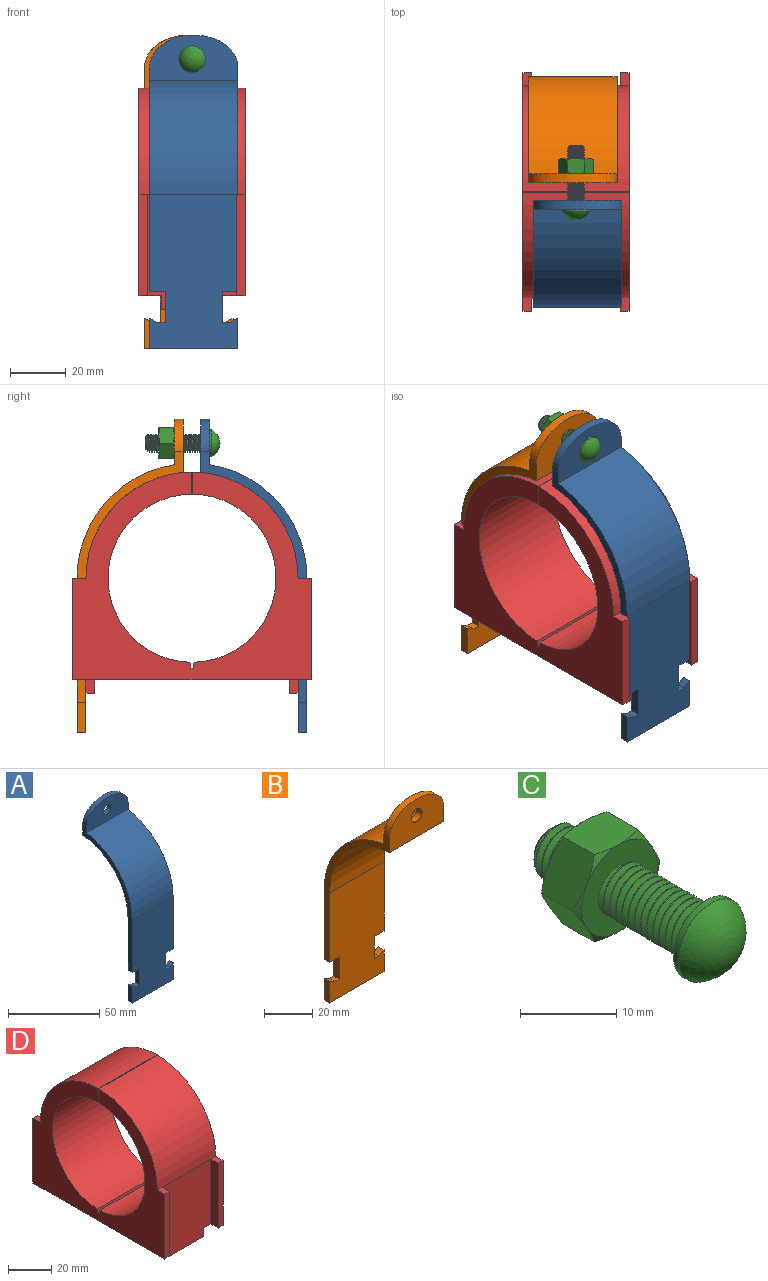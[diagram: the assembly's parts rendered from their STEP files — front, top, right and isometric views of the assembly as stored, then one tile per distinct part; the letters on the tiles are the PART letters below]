
ASSEMBLY  parts=4 mates=3
PART A: 21 faces, bbox 31.8x38.1x112.7 mm
  f0: plane 80.68x38.1mm, normal (-1,0,0), area 313.9mm2, adj f1,f13,f14,f15,f16,f17,f18,f20
  f1: plane 5.55x3.18mm, normal (0,0,-1), area 17.6mm2, adj f0,f2,f13,f16
  f2: plane 11.13x3.18mm, normal (-1,0,0), area 35.3mm2, adj f1,f3,f13,f16
  f3: plane 3.18x2.54mm, normal (0,0,1), area 8.1mm2, adj f2,f4,f13,f16
  f4: plane 3.18x3.01mm, normal (0.47,0,0.89), area 10.8mm2, adj f3,f5,f13,f16
  f5: plane 10.97x3.18mm, normal (-1,0,0), area 34.8mm2, adj f4,f6,f13,f16
  f6: plane 31.75x3.18mm, normal (0,0,-1), area 100.8mm2, adj f5,f7,f13,f16
  f7: plane 10.97x3.18mm, normal (1,0,0), area 34.8mm2, adj f6,f8,f13,f16
  f8: plane 3.18x3.01mm, normal (-0.47,0,0.89), area 10.8mm2, adj f7,f9,f13,f16
  f9: plane 3.18x2.54mm, normal (0,0,1), area 8.1mm2, adj f8,f10,f13,f16
  f10: plane 11.13x3.18mm, normal (1,0,0), area 35.3mm2, adj f9,f11,f13,f16
  f11: plane 5.55x3.18mm, normal (0,0,-1), area 17.6mm2, adj f10,f12,f13,f16
  f12: plane 80.68x38.1mm, normal (1,0,0), area 313.9mm2, adj f11,f13,f14,f15,f16,f17,f18,f20
  f13: plane 55.55x31.75mm, normal (0,-1,0), area 1645mm2, adj f0,f1,f2,f3,f4,f5,f6,f7
  f14: plane 31.75x16.38mm, normal (0,-1,0), area 409.9mm2, adj f0,f12,f15,f19,f20
  f15: cylinder r=41.27mm len=40.78mm, axis (1,0,0), area 1856.1mm2, adj f0,f12,f13,f14
  f16: plane 55.55x31.75mm, normal (0,1,0), area 1645mm2, adj f0,f1,f2,f3,f4,f5,f6,f7
  f17: cylinder r=38.1mm len=37.97mm, axis (1,0,0), area 1799.2mm2, adj f0,f12,f16,f18
  f18: plane 31.75x19.2mm, normal (0,1,0), area 499.3mm2, adj f0,f12,f17,f19,f20
  f19: cylinder r=3.17mm len=6.35mm, axis (0,-1,0), area 63.3mm2, adj f14,f18
  f20: extruded ~31.75x11.52mm, area 137.5mm2, adj f0,f12,f14,f18
PART B: 21 faces, bbox 31.8x38.1x112.7 mm
  f0: plane 80.68x38.1mm, normal (-1,0,0), area 313.9mm2, adj f1,f13,f14,f15,f16,f17,f18,f20
  f1: plane 55.55x31.75mm, normal (0,1,0), area 1645mm2, adj f0,f2,f3,f4,f5,f6,f7,f8
  f2: plane 80.68x38.1mm, normal (1,0,0), area 313.9mm2, adj f1,f3,f14,f15,f16,f17,f18,f20
  f3: plane 5.55x3.18mm, normal (0,0,-1), area 17.6mm2, adj f1,f2,f4,f14
  f4: plane 11.13x3.18mm, normal (1,0,0), area 35.3mm2, adj f1,f3,f5,f14
  f5: plane 3.18x2.54mm, normal (0,0,1), area 8.1mm2, adj f1,f4,f6,f14
  f6: plane 3.18x3.01mm, normal (-0.47,0,0.89), area 10.8mm2, adj f1,f5,f7,f14
  f7: plane 10.97x3.18mm, normal (1,0,0), area 34.8mm2, adj f1,f6,f8,f14
  f8: plane 31.75x3.18mm, normal (0,0,-1), area 100.8mm2, adj f1,f7,f9,f14
  f9: plane 10.97x3.18mm, normal (-1,0,0), area 34.8mm2, adj f1,f8,f10,f14
  f10: plane 3.18x3.01mm, normal (0.47,0,0.89), area 10.8mm2, adj f1,f9,f11,f14
  f11: plane 3.18x2.54mm, normal (0,0,1), area 8.1mm2, adj f1,f10,f12,f14
  f12: plane 11.13x3.18mm, normal (-1,0,0), area 35.3mm2, adj f1,f11,f13,f14
  f13: plane 5.55x3.18mm, normal (0,0,-1), area 17.6mm2, adj f0,f1,f12,f14
  f14: plane 55.55x31.75mm, normal (0,-1,0), area 1645mm2, adj f0,f2,f3,f4,f5,f6,f7,f8
  f15: cylinder r=38.1mm len=37.97mm, axis (1,0,0), area 1799.2mm2, adj f0,f2,f14,f16
  f16: plane 31.75x19.2mm, normal (0,-1,0), area 499.3mm2, adj f0,f2,f15,f19,f20
  f17: cylinder r=41.27mm len=40.78mm, axis (1,0,0), area 1856.1mm2, adj f0,f1,f2,f18
  f18: plane 31.75x16.38mm, normal (0,1,0), area 409.9mm2, adj f0,f2,f17,f19,f20
  f19: cylinder r=3.17mm len=6.35mm, axis (0,-1,0), area 63.3mm2, adj f16,f18
  f20: extruded ~31.75x11.52mm, area 137.5mm2, adj f0,f2,f16,f18
PART C: 34 faces, bbox 13.4x27.4x13.4 mm
  f0: cylinder r=3.17mm len=12.7mm, axis (0,-1,0), area 31.8mm2, adj f1,f3,f4,f8
  f1: bspline ~13.49x6.35mm, area 172.8mm2, adj f0,f2,f4,f8
  f2: cylinder r=2.59mm len=12.7mm, axis (0,-1,0), area 25.9mm2, adj f1,f3,f4,f8
  f3: bspline ~13.49x6.35mm, area 172.8mm2, adj f0,f2,f4,f8
  f4: plane 9.89x9.89mm, normal (0,1,0), area 45.1mm2, adj f0,f1,f2,f3,f5
  f5: cylinder r=4.76mm len=9.53mm, axis (0,1,0), area 22.8mm2, adj f4,f6
  f6: sphere r=5.32mm, area 98.5mm2, adj f5
  f7: plane 11.47x11.47mm, normal (0,1,0), area 70.8mm2, adj f15,f16,f17,f18,f19,f20,f30,f31
  f8: plane 11.47x11.47mm, normal (0,-1,0), area 70.8mm2, adj f0,f1,f2,f3,f21,f22,f23,f24
  f9: plane 6.09x6.08mm, normal (-0.87,0,0.5), area 33.4mm2, adj f10,f14,f15,f20,f21,f26
  f10: plane 6.95x6.08mm, normal (0,0,1), area 33.4mm2, adj f9,f11,f19,f20,f25,f26
  f11: plane 6.09x6.08mm, normal (0.87,0,0.5), area 33.4mm2, adj f10,f12,f18,f19,f24,f25
  f12: plane 6.09x6.08mm, normal (0.87,0,-0.5), area 33.4mm2, adj f11,f13,f17,f18,f23,f24
  f13: plane 6.95x6.08mm, normal (0,0,-1), area 33.4mm2, adj f12,f14,f16,f17,f22,f23
  f14: plane 6.09x6.08mm, normal (-0.87,0,-0.5), area 33.4mm2, adj f9,f13,f15,f16,f21,f22
  f15: cone r=5.56mm half-angle=60deg, axis (0,-1,0), area 3mm2, adj f7,f9,f14
  f16: cone r=5.56mm half-angle=60deg, axis (0,-1,0), area 3mm2, adj f7,f13,f14
  f17: cone r=5.56mm half-angle=60deg, axis (0,-1,0), area 3mm2, adj f7,f12,f13
  f18: cone r=5.56mm half-angle=60deg, axis (0,-1,0), area 3mm2, adj f7,f11,f12
  f19: cone r=5.56mm half-angle=60deg, axis (0,-1,0), area 3mm2, adj f7,f10,f11
  f20: cone r=5.56mm half-angle=60deg, axis (0,-1,0), area 3mm2, adj f7,f9,f10
  f21: cone r=5.56mm half-angle=60deg, axis (0,1,0), area 3mm2, adj f8,f9,f14
  f22: cone r=5.56mm half-angle=60deg, axis (0,1,0), area 3mm2, adj f8,f13,f14
  f23: cone r=5.56mm half-angle=60deg, axis (0,1,0), area 3mm2, adj f8,f12,f13
  f24: cone r=5.56mm half-angle=60deg, axis (0,1,0), area 3mm2, adj f8,f11,f12
  f25: cone r=5.56mm half-angle=60deg, axis (0,1,0), area 3mm2, adj f8,f10,f11
  f26: cone r=5.56mm half-angle=60deg, axis (0,1,0), area 3mm2, adj f8,f9,f10
  f27: plane 4.54x4.54mm, normal (0,1,0), area 16.2mm2, adj f28
  f28: cone r=3.17mm half-angle=45deg, axis (0,-1,0), area 12.5mm2, adj f27,f29,f30,f31,f32
  f29: cone r=3.17mm half-angle=45deg, axis (0,-1,0), area 1.7mm2, adj f28,f30,f32,f33
  f30: bspline ~6.35x6.35mm, area 56.5mm2, adj f7,f28,f29,f31,f33
  f31: cylinder r=2.59mm len=5.17mm, axis (0,-1,0), area 9.1mm2, adj f7,f28,f30,f32
  f32: bspline ~6.35x6.35mm, area 56.2mm2, adj f7,f28,f29,f31,f33
  f33: cylinder r=3.17mm len=6.35mm, axis (0,-1,0), area 9.6mm2, adj f7,f29,f30,f32
PART D: 35 faces, bbox 38.1x85.7x79.4 mm
  f0: plane 36.51x3.18mm, normal (0,-1,0), area 115.9mm2, adj f1,f11,f25,f30
  f1: plane 4.76x3.18mm, normal (0,0,1), area 15.1mm2, adj f0,f23,f25,f30
  f2: plane 36.51x3.18mm, normal (0,1,0), area 115.9mm2, adj f3,f11,f25,f28
  f3: plane 4.76x3.18mm, normal (0,0,1), area 15.1mm2, adj f2,f14,f25,f28
  f4: plane 36.51x3.18mm, normal (0,-1,0), area 115.9mm2, adj f11,f24,f26,f29
  f5: plane 41.28x31.75mm, normal (0,-1,0), area 1264.9mm2, adj f6,f11,f23,f29,f30,f31,f33
  f6: plane 22.17x3.18mm, normal (0,0,-1), area 70.4mm2, adj f5,f7,f31,f33
  f7: plane 22.17x4.76mm, normal (0,1,0), area 105.6mm2, adj f6,f11,f31,f33
  f8: plane 22.17x4.76mm, normal (0,-1,0), area 105.6mm2, adj f9,f11,f32,f34
  f9: plane 22.17x3.18mm, normal (0,0,-1), area 70.4mm2, adj f8,f10,f32,f34
  f10: plane 41.28x31.75mm, normal (0,1,0), area 1264.9mm2, adj f9,f11,f14,f27,f28,f32,f34
  f11: plane 85.73x38.1mm, normal (0,0,-1), area 2822.9mm2, adj f0,f2,f4,f5,f7,f8,f10,f12
  f12: plane 36.51x3.18mm, normal (0,1,0), area 115.9mm2, adj f11,f13,f26,f27
  f13: plane 4.76x3.18mm, normal (0,0,1), area 15.1mm2, adj f12,f14,f26,f27
  f14: cylinder r=38.1mm len=38.1mm, axis (-1,0,0), area 2275.3mm2, adj f3,f10,f13,f15,f25,f26
  f15: plane 38.1x7.94mm, normal (0,-1,0), area 302.4mm2, adj f14,f16,f25,f26
  f16: cylinder r=30.16mm len=60.32mm, axis (-1,0,0), area 3577.9mm2, adj f15,f17,f25,f26
  f17: plane 38.1x2.12mm, normal (0,-0.99,0.15), area 81.6mm2, adj f16,f18,f25,f26
  f18: plane 38.1x0.39mm, normal (0,-0.25,0.97), area 15.5mm2, adj f17,f19,f25,f26
  f19: plane 38.1x0.39mm, normal (0,0.25,0.97), area 15.5mm2, adj f18,f20,f25,f26
  f20: plane 38.1x2.12mm, normal (0,0.99,0.15), area 81.6mm2, adj f19,f21,f25,f26
  f21: cylinder r=30.16mm len=60.32mm, axis (-1,0,0), area 3577.9mm2, adj f20,f22,f25,f26
  f22: plane 38.1x7.94mm, normal (0,1,0), area 302.4mm2, adj f21,f23,f25,f26
  f23: cylinder r=38.1mm len=38.1mm, axis (-1,0,0), area 2275.3mm2, adj f1,f5,f22,f24,f25,f26
  f24: plane 4.76x3.18mm, normal (0,0,1), area 15.1mm2, adj f4,f23,f26,f29
  f25: plane 85.73x74.61mm, normal (1,0,0), area 2547.7mm2, adj f0,f1,f2,f3,f11,f14,f15,f16
  f26: plane 85.73x74.61mm, normal (-1,0,0), area 2547.7mm2, adj f4,f11,f12,f13,f14,f15,f16,f17
  f27: plane 36.51x4.76mm, normal (1,0,0), area 173.9mm2, adj f10,f11,f12,f13
  f28: plane 36.51x4.76mm, normal (-1,0,0), area 173.9mm2, adj f2,f3,f10,f11
  f29: plane 36.51x4.76mm, normal (1,0,0), area 173.9mm2, adj f4,f5,f11,f24
  f30: plane 36.51x4.76mm, normal (-1,0,0), area 173.9mm2, adj f0,f1,f5,f11
  f31: plane 4.76x3.18mm, normal (-1,0,0), area 15.1mm2, adj f5,f6,f7,f11
  f32: plane 4.76x3.18mm, normal (-1,0,0), area 15.1mm2, adj f8,f9,f10,f11
  f33: plane 4.76x3.18mm, normal (1,0,0), area 15.1mm2, adj f5,f6,f7,f11
  f34: plane 4.76x3.18mm, normal (1,0,0), area 15.1mm2, adj f8,f9,f10,f11
PLACE A t=(-63.94,-35.8,-34.76)mm
PLACE B t=(-65.72,-35.8,-34.76)mm
PLACE C t=(-64.58,-35.8,-35.23)mm
PLACE D t=(-64.58,-35.8,-34.76)mm
MATE fastened D.f14 <-> B.f15  axis (1,0,0) through (-45.53,-35.8,-34.76)mm
MATE fastened A.f19 <-> C.f4  axis (0,-1,0) through (-63.94,-42.15,14.22)mm
MATE fastened A.f15 <-> D.f14  axis (1,0,0) through (-48.07,-35.8,-34.76)mm
